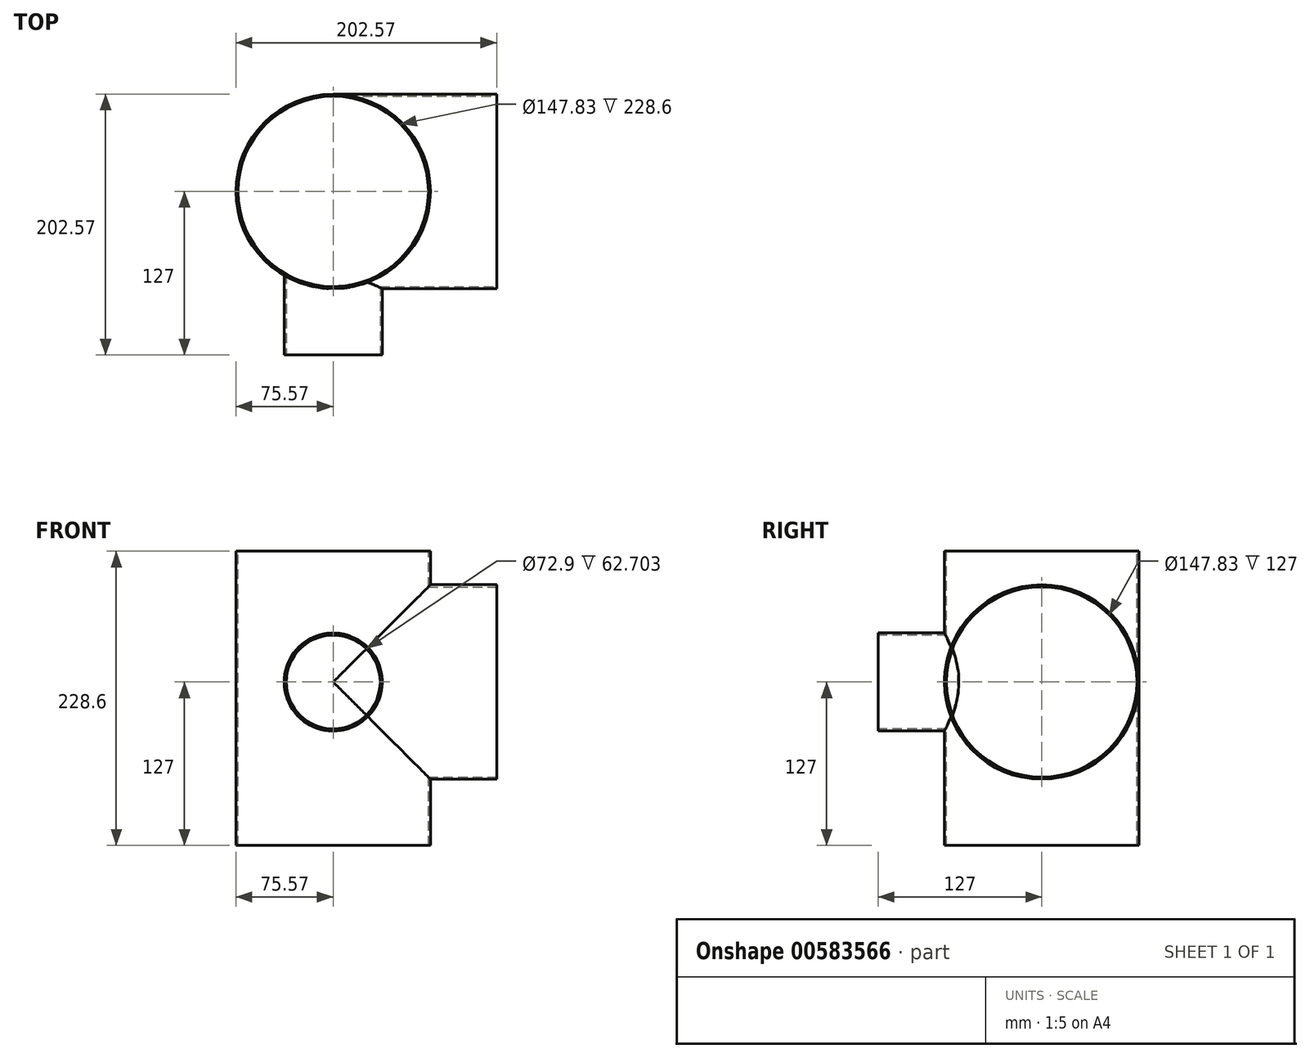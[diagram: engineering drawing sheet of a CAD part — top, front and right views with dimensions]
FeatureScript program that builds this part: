
annotation { "Feature Type Name" : "Feature", "Feature Type Description" : "" }
export const myFeature = defineFeature(function(context is Context, id is Id, definition is map)
    precondition{}
    {
        {
            var Q0;
            Q0=qCreatedBy(makeId("Top.planeOp"),FACE);
            var sketch = newSketch(context, id + "F0", { "sketchPlane" : qUnion([Q0])});
            skCircle(sketch, "E0", {"center": v(0, 0) * mm, "radius": 75.56 * mm});
            skSolve(sketch);
        }
        {
            var Q0;
            Q0=makeQuery(id+"F0.imprint","IMPRINT",FACE,{"disambiguationData":[TD([[makeQuery(id+"F0.imprint","IMPRINT",EDGE,{"derivedFrom":sQuery(id+"F0.wireOp",EDGE,"E0")}),1.0]])]});
            extrude(context, id + "F1", {"entities" : qUnion([Q0]), "depth" : 101.6 * mm, "offsetDistance" : 25.4 * mm});
        }
        {
            var Q0;
            Q0 = qSketchRegion(id + "F0", true);
            extrude(context, id + "F2", {"entities" : qUnion([Q0]), "operationType" : NewBodyOperationType.ADD, "oppositeDirection" : true, "depth" : 127 * mm, "offsetDistance" : 25.4 * mm});
        }
        {
            var Q0;
            Q0=qCreatedBy(makeId("Front.planeOp"),FACE);
            var sketch = newSketch(context, id + "F3", { "sketchPlane" : qUnion([Q0])});
            skCircle(sketch, "E1", {"center": v(0, 0) * mm, "radius": 38.1 * mm});
            skSolve(sketch);
        }
        {
            var Q0;
            Q0 = qSketchRegion(id + "F3", true);
            extrude(context, id + "F4", {"entities" : qUnion([Q0]), "operationType" : NewBodyOperationType.ADD, "depth" : 127 * mm, "offsetDistance" : 25.4 * mm});
        }
        {
            var Q0;
            Q0=qCreatedBy(makeId("Right.planeOp"),FACE);
            var sketch = newSketch(context, id + "F5", { "sketchPlane" : qUnion([Q0])});
            skCircle(sketch, "E2", {"center": v(0, 0) * mm, "radius": 75.56 * mm});
            skSolve(sketch);
        }
        {
            var Q0;
            Q0 = qSketchRegion(id + "F5", true);
            extrude(context, id + "F6", {"entities" : qUnion([Q0]), "operationType" : NewBodyOperationType.ADD, "depth" : 127 * mm, "offsetDistance" : 25.4 * mm});
        }
        {
            var Q0;
            Q0=makeQuery(id+"F1.opExtrude","CAP_FACE",FACE,{"disambiguationData":[OSD([sQuery(id+"F0.wireOp",EDGE,"E0")])],"isStart":false});
            var sketch = newSketch(context, id + "F7", { "sketchPlane" : qUnion([Q0])});
            skCircle(sketch, "E3", {"center": v(0, 0) * mm, "radius": 73.91 * mm});
            skSolve(sketch);
        }
        {
            var Q0;
            Q0=makeQuery(id+"F7.imprint","IMPRINT",FACE,{"disambiguationData":[TD([[makeQuery(id+"F7.imprint","IMPRINT",EDGE,{"derivedFrom":sQuery(id+"F7.wireOp",EDGE,"E3")}),1.0]])]});
            extrude(context, id + "F8", {"entities" : qUnion([Q0]), "operationType" : NewBodyOperationType.REMOVE, "endBound" : BoundingType.THROUGH_ALL, "oppositeDirection" : true, "depth" : 25.4 * mm, "offsetDistance" : 25.4 * mm});
        }
        {
            var Q0;
            Q0=makeQuery(id+"F6.opExtrude","CAP_FACE",FACE,{"disambiguationData":[OSD([sQuery(id+"F5.wireOp",EDGE,"E2")])],"isStart":false});
            var sketch = newSketch(context, id + "F9", { "sketchPlane" : qUnion([Q0])});
            skCircle(sketch, "E4", {"center": v(0, 0) * mm, "radius": 73.91 * mm});
            skSolve(sketch);
        }
        {
            var Q0;
            Q0 = qSketchRegion(id + "F9", true);
            extrude(context, id + "F10", {"entities" : qUnion([Q0]), "operationType" : NewBodyOperationType.REMOVE, "endBound" : BoundingType.UP_TO_NEXT, "oppositeDirection" : true, "depth" : 25.4 * mm, "offsetDistance" : 25.4 * mm});
        }
        {
            var Q0;
            Q0=makeQuery(id+"F4.opExtrude","CAP_FACE",FACE,{"disambiguationData":[OSD([sQuery(id+"F3.wireOp",EDGE,"E1")])],"isStart":false});
            var sketch = newSketch(context, id + "F11", { "sketchPlane" : qUnion([Q0])});
            skCircle(sketch, "E5", {"center": v(0, 0) * mm, "radius": 36.45 * mm});
            skSolve(sketch);
        }
        {
            var Q0;
            Q0 = qSketchRegion(id + "F11", true);
            extrude(context, id + "F12", {"entities" : qUnion([Q0]), "operationType" : NewBodyOperationType.REMOVE, "endBound" : BoundingType.UP_TO_NEXT, "oppositeDirection" : true, "depth" : 25.4 * mm, "offsetDistance" : 25.4 * mm});
        }
    });
